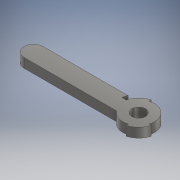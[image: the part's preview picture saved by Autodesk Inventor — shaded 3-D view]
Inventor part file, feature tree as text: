
AUTODESK INVENTOR PART (.ipt)
format: ipt  version: 2018 (Build 220112000, 112)  size: 131,584 bytes
history: native  units: mm
features: extrude x1, sketch x1
ambient origin geometry x8: Origin, YZ Plane, XZ Plane, XY Plane, X Axis, Y Axis, Z Axis, Center Point
bodies: Solid1 (feature_tree)
feature tree (2):
  extrude  "Extrusion1"  Depth=9.0mm
  sketch  "Sketch1"  dims[d0=13.0mm d1=30.0mm d2=42.0mm d3=34.0mm d4=4.5mm d5=4.5mm d6=4.5mm d7=4.5mm d8=100.0mm d9=9.0mm d10=9.0mm d11=0.0mm]
